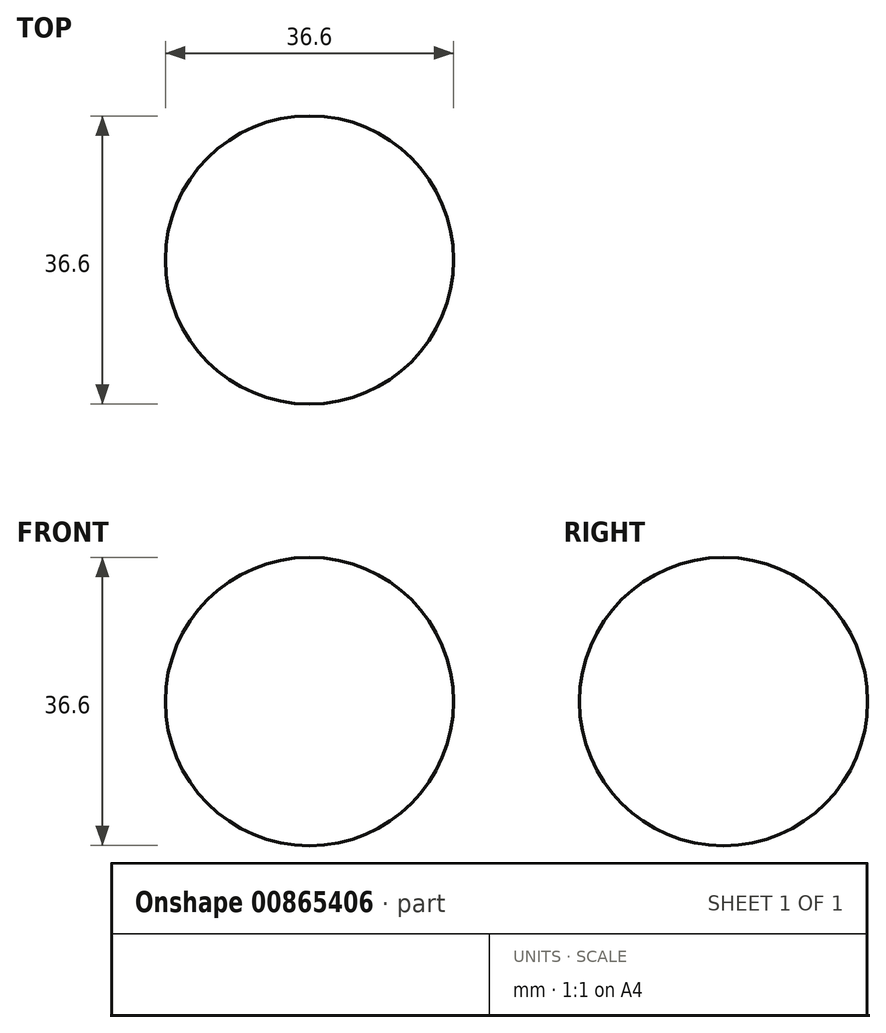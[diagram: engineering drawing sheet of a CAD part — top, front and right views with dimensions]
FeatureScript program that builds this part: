
annotation { "Feature Type Name" : "Feature", "Feature Type Description" : "" }
export const myFeature = defineFeature(function(context is Context, id is Id, definition is map)
    precondition{}
    {
        {
            var Q0;
            Q0=qCreatedBy(makeId("Top.planeOp"),FACE);
            var sketch = newSketch(context, id + "F0", { "sketchPlane" : qUnion([Q0])});
            skCircle(sketch, "E0", {"center": v(0, 0) * mm, "radius": 18.3 * mm});
            skLineSegment(sketch, "E1", {"start": v(0, 0) * mm, "end": v(-18.3, 0) * mm, "construction": true});
            skLineSegment(sketch, "E2", {"start": v(-18.3, 0) * mm, "end": v(18.3, 0) * mm});
            skSolve(sketch);
        }
        {
            var Q0;
            {var subQ0=sQuery(id+"F0.wireOp",EDGE,"E2");Q0=makeQuery(id+"F0.imprint","IMPRINT",FACE,{"disambiguationData":[TD([[makeQuery(id+"F0.imprint","IMPRINT",EDGE,{"derivedFrom":subQ0}),-1.0]])]});}
            var Q1;
            Q1=sQuery(id+"F0.wireOp",EDGE,"E2");
            revolve(context, id + "F1", {"surfaceOperationType" : NewSurfaceOperationType.NEW, "entities" : qUnion([Q0]), "axis" : qUnion([Q1]), "revolveType" : RevolveType.FULL});
        }
    });
